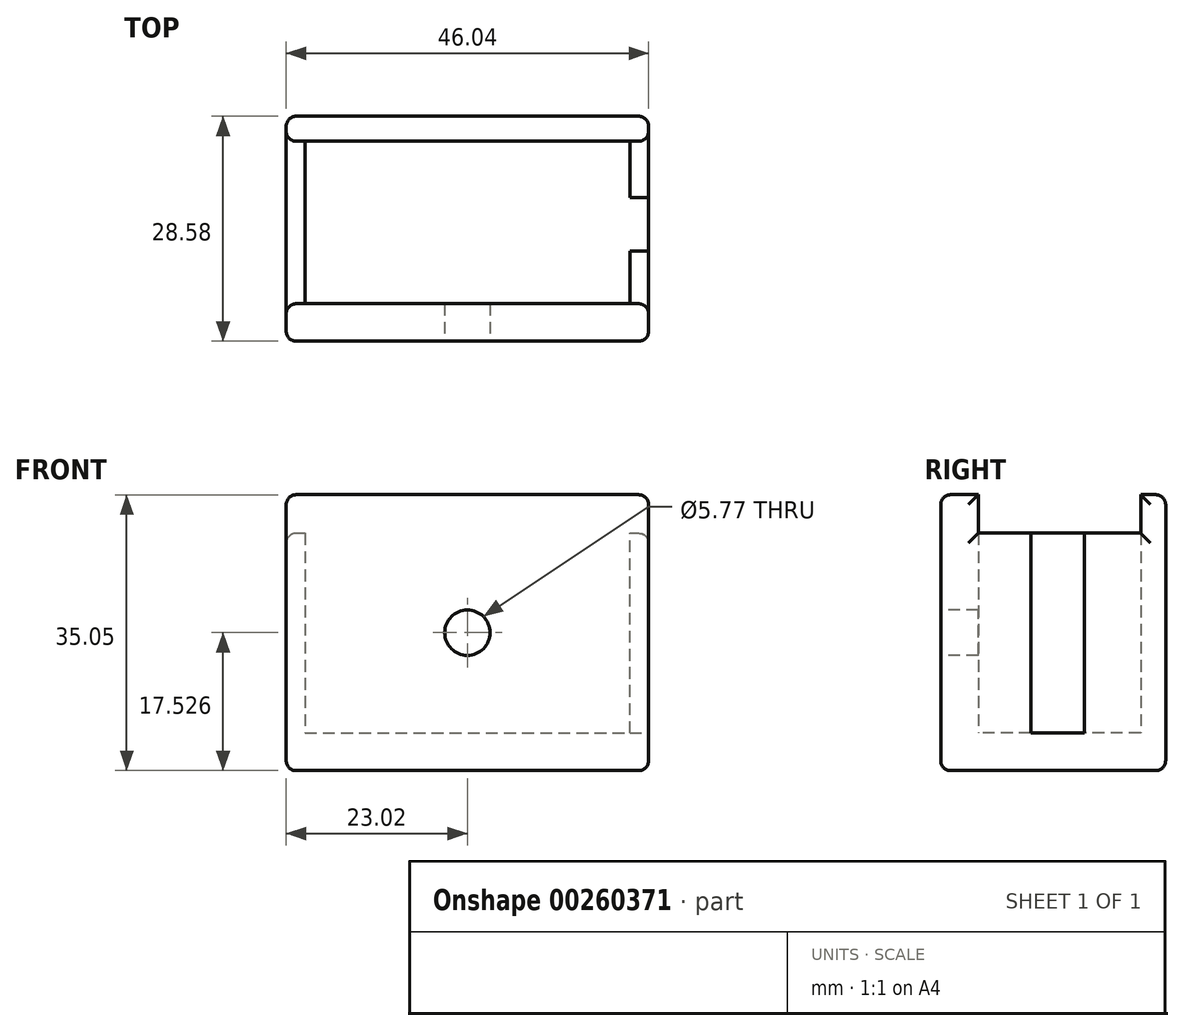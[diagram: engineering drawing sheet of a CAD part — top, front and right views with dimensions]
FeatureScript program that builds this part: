
annotation { "Feature Type Name" : "Feature", "Feature Type Description" : "" }
export const myFeature = defineFeature(function(context is Context, id is Id, definition is map)
    precondition{}
    {
        {
            var Q0;
            Q0=qCreatedBy(makeId("Top.planeOp"),FACE);
            var sketch = newSketch(context, id + "F0", { "sketchPlane" : qUnion([Q0])});
            skLineSegment(sketch, "E0.bottom", {"start": v(23.02, 14.29) * mm, "end": v(-23.02, 14.29) * mm});
            skLineSegment(sketch, "E0.top", {"start": v(23.02, -14.29) * mm, "end": v(-23.02, -14.29) * mm});
            skLineSegment(sketch, "E0.left", {"start": v(23.02, 14.29) * mm, "end": v(23.02, -14.29) * mm});
            skLineSegment(sketch, "E0.right", {"start": v(-23.02, 14.29) * mm, "end": v(-23.02, -14.29) * mm});
            skPoint(sketch, "E0.middle", {"position": v(0, 0) * mm});
            skSolve(sketch);
        }
        {
            var Q0;
            Q0=makeQuery(id+"F0.imprint","IMPRINT",FACE,{"disambiguationData":[TD([[makeQuery(id+"F0.imprint","IMPRINT",EDGE,{"derivedFrom":sQuery(id+"F0.wireOp",EDGE,"E0.bottom")}),1.0]])]});
            extrude(context, id + "F1", {"entities" : qUnion([Q0]), "depth" : 4.76 * mm});
        }
        {
            var Q0;
            Q0=makeQuery(id+"F1.opExtrude","CAP_FACE",FACE,{"disambiguationData":[OSD([sQuery(id+"F0.wireOp",EDGE,"E0.bottom"),sQuery(id+"F0.wireOp",EDGE,"E0.top"),sQuery(id+"F0.wireOp",EDGE,"E0.left"),sQuery(id+"F0.wireOp",EDGE,"E0.right")])],"isStart":false});
            var sketch = newSketch(context, id + "F2", { "sketchPlane" : qUnion([Q0])});
            skLineSegment(sketch, "E1.bottom", {"start": v(-23.02, -14.29) * mm, "end": v(23.02, -14.29) * mm});
            skLineSegment(sketch, "E1.top", {"start": v(-23.02, -9.53) * mm, "end": v(23.02, -9.53) * mm});
            skLineSegment(sketch, "E1.left", {"start": v(-23.02, -14.29) * mm, "end": v(-23.02, -9.53) * mm});
            skLineSegment(sketch, "E1.right", {"start": v(23.02, -14.29) * mm, "end": v(23.02, -9.53) * mm});
            skLineSegment(sketch, "E2.bottom", {"start": v(-23.02, 14.29) * mm, "end": v(23.02, 14.29) * mm});
            skLineSegment(sketch, "E2.top", {"start": v(-23.02, 11.11) * mm, "end": v(23.02, 11.11) * mm});
            skLineSegment(sketch, "E2.left", {"start": v(-23.02, 14.29) * mm, "end": v(-23.02, 11.11) * mm});
            skLineSegment(sketch, "E2.right", {"start": v(23.02, 14.29) * mm, "end": v(23.02, 11.11) * mm});
            skLineSegment(sketch, "E3.bottom", {"start": v(-23.02, 11.11) * mm, "end": v(-20.64, 11.11) * mm});
            skLineSegment(sketch, "E3.top", {"start": v(-23.02, -9.53) * mm, "end": v(-20.64, -9.53) * mm});
            skLineSegment(sketch, "E3.left", {"start": v(-23.02, 11.11) * mm, "end": v(-23.02, -9.53) * mm});
            skLineSegment(sketch, "E3.right", {"start": v(-20.64, 11.11) * mm, "end": v(-20.64, -9.53) * mm});
            skLineSegment(sketch, "E4.bottom", {"start": v(23.02, 11.11) * mm, "end": v(20.64, 11.11) * mm});
            skLineSegment(sketch, "E4.top", {"start": v(23.02, -9.53) * mm, "end": v(20.64, -9.53) * mm});
            skLineSegment(sketch, "E4.left", {"start": v(23.02, 11.11) * mm, "end": v(23.02, -9.53) * mm});
            skLineSegment(sketch, "E4.right", {"start": v(20.64, 11.11) * mm, "end": v(20.64, -9.53) * mm});
            skSolve(sketch);
        }
        {
            var Q0;
            Q0=makeQuery(id+"F2.imprint","IMPRINT",FACE,{"disambiguationData":[TD([[makeQuery(id+"F2.imprint","IMPRINT",EDGE,{"derivedFrom":sQuery(id+"F2.wireOp",EDGE,"E1.bottom")}),-1.0]])]});
            var Q1;
            Q1=makeQuery(id+"F2.imprint","IMPRINT",FACE,{"disambiguationData":[TD([[makeQuery(id+"F2.imprint","IMPRINT",EDGE,{"derivedFrom":sQuery(id+"F2.wireOp",EDGE,"E2.bottom")}),1.0]])]});
            extrude(context, id + "F3", {"entities" : qUnion([Q0, Q1]), "operationType" : NewBodyOperationType.ADD, "depth" : 30.29 * mm});
        }
        {
            var Q0;
            Q0 = qSketchRegion(id + "F2", true);
            extrude(context, id + "F4", {"entities" : qUnion([Q0]), "operationType" : NewBodyOperationType.ADD, "depth" : 25.4 * mm});
        }
        {
            var Q0;
            {var subQ0=sQuery(id+"F2.wireOp",EDGE,"E2.right");var subQ1=sQuery(id+"F2.wireOp",EDGE,"E1.right");Q0=makeQuery(id+"F4.boolean.opBoolean","MERGE",FACE,{"derivedFrom":[makeQuery(id+"F3.boolean.opBoolean","MERGE",FACE,{"derivedFrom":[makeQuery(id+"F1.opExtrude","SWEPT_FACE",FACE,{"disambiguationData":[OSD([sQuery(id+"F0.wireOp",EDGE,"E0.left")])]}),makeQuery(id+"F3.opExtrude","SWEPT_FACE",FACE,{"disambiguationData":[OSD([subQ1])]}),makeQuery(id+"F3.opExtrude","SWEPT_FACE",FACE,{"disambiguationData":[OSD([subQ0])]})]}),makeQuery(id+"F4.opExtrude","SWEPT_FACE",FACE,{"disambiguationData":[OSD([subQ1,subQ0,sQuery(id+"F2.wireOp",EDGE,"E4.left")])]})]});}
            var sketch = newSketch(context, id + "F5", { "sketchPlane" : qUnion([Q0])});
            skLineSegment(sketch, "E5.top", {"start": v(0.35, 30.16) * mm, "end": v(3.97, 30.16) * mm});
            skLineSegment(sketch, "E5.right", {"start": v(3.97, 16.57) * mm, "end": v(3.97, 30.16) * mm});
            skLineSegment(sketch, "E6.top", {"start": v(3.97, 4.76) * mm, "end": v(0.35, 4.76) * mm});
            skLineSegment(sketch, "E6.left", {"start": v(3.97, 16.57) * mm, "end": v(3.97, 4.76) * mm});
            skLineSegment(sketch, "E7.bottom", {"start": v(0.35, 30.16) * mm, "end": v(-2.83, 30.16) * mm});
            skLineSegment(sketch, "E7.right", {"start": v(-2.83, 30.16) * mm, "end": v(-2.83, 16.57) * mm});
            skLineSegment(sketch, "E8.top", {"start": v(0.35, 4.76) * mm, "end": v(-2.83, 4.76) * mm});
            skLineSegment(sketch, "E8.right", {"start": v(-2.83, 11.8) * mm, "end": v(-2.83, 4.76) * mm});
            skLineSegment(sketch, "E9", {"start": v(-2.83, 16.57) * mm, "end": v(-2.83, 11.8) * mm});
            skSolve(sketch);
        }
        {
            var Q0;
            Q0=makeQuery(id+"F5.imprint","IMPRINT",FACE,{"disambiguationData":[TD([[makeQuery(id+"F5.imprint","IMPRINT",EDGE,{"derivedFrom":sQuery(id+"F5.wireOp",EDGE,"sFapN1J0-1lHc-71WO-3CpR-hcseuhe5HOpb.bottom")}),-1.0]])]});
            var Q1;
            Q1=makeQuery(id+"F5.imprint","IMPRINT",FACE,{"disambiguationData":[TD([[makeQuery(id+"F5.imprint","IMPRINT",EDGE,{"derivedFrom":sQuery(id+"F5.wireOp",EDGE,"E5.top")}),1.0]])]});
            extrude(context, id + "F6", {"entities" : qUnion([Q0, Q1]), "operationType" : NewBodyOperationType.REMOVE, "endBound" : BoundingType.UP_TO_NEXT, "oppositeDirection" : true, "depth" : 25.4 * mm});
        }
        {
            var Q0;
            Q0=makeQuery(id+"F3.boolean.opBoolean","MERGE",FACE,{"derivedFrom":[makeQuery(id+"F1.opExtrude","SWEPT_FACE",FACE,{"disambiguationData":[OSD([sQuery(id+"F0.wireOp",EDGE,"E0.top")])]}),makeQuery(id+"F3.opExtrude","SWEPT_FACE",FACE,{"disambiguationData":[OSD([sQuery(id+"F2.wireOp",EDGE,"E1.bottom")])]})]});
            var sketch = newSketch(context, id + "F7", { "sketchPlane" : qUnion([Q0])});
            skLineSegment(sketch, "E10", {"start": v(-23.02, 17.53) * mm, "end": v(23.02, 17.53) * mm});
            skLineSegment(sketch, "E11", {"start": v(0, 0) * mm, "end": v(0, 35.05) * mm});
            skPoint(sketch, "E12", {"position": v(0, 17.53) * mm});
            skSolve(sketch);
        }
        {
            var Q0;
            Q0=sQuery(id+"F7.wireOp",VERTEX,"E12");
            var Q1;
            Q1=makeQuery(id+"F1.opExtrude","SWEPT_BODY",BODY,{"disambiguationData":[OSD([sQuery(id+"F0.wireOp",EDGE,"E0.bottom"),sQuery(id+"F0.wireOp",EDGE,"E0.top"),sQuery(id+"F0.wireOp",EDGE,"E0.left"),sQuery(id+"F0.wireOp",EDGE,"E0.right")])]});
            hole(context, id + "F8", {"style" : HoleStyle.SIMPLE, "endStyle" : HoleEndStyle.BLIND, "holeDiameter" : 5.77 * mm, "holeDepth" : 4.76 * mm, "tappedDepth" : 12.7 * mm, "tapClearance" : 3, "startFromSketch" : true, "locations" : qUnion([Q0]), "scope" : qUnion([Q1])});
        }
        {
            var Q0;
            Q0=makeQuery(id+"F3.boolean.opBoolean","MERGE",EDGE,{"derivedFrom":[makeQuery(id+"F1.opExtrude","SWEPT_EDGE",EDGE,{"disambiguationData":[OSD([sQuery(id+"F0.wireOp",EDGE,"E0.bottom"),sQuery(id+"F0.wireOp",EDGE,"E0.left")])]}),makeQuery(id+"F3.opExtrude","SWEPT_EDGE",EDGE,{"disambiguationData":[OSD([sQuery(id+"F2.wireOp",EDGE,"E2.bottom"),sQuery(id+"F2.wireOp",EDGE,"E2.right")])]})]});
            var Q1;
            Q1=makeQuery(id+"F3.boolean.opBoolean","MERGE",EDGE,{"derivedFrom":[makeQuery(id+"F1.opExtrude","SWEPT_EDGE",EDGE,{"disambiguationData":[OSD([sQuery(id+"F0.wireOp",EDGE,"E0.bottom"),sQuery(id+"F0.wireOp",EDGE,"E0.right")])]}),makeQuery(id+"F3.opExtrude","SWEPT_EDGE",EDGE,{"disambiguationData":[OSD([sQuery(id+"F2.wireOp",EDGE,"E2.bottom"),sQuery(id+"F2.wireOp",EDGE,"E2.left")])]})]});
            var Q2;
            Q2=makeQuery(id+"F3.opExtrude","CAP_EDGE",EDGE,{"disambiguationData":[OSD([sQuery(id+"F2.wireOp",EDGE,"E2.bottom")])],"isStart":false});
            var Q3;
            Q3=makeQuery(id+"F1.opExtrude","CAP_EDGE",EDGE,{"disambiguationData":[OSD([sQuery(id+"F0.wireOp",EDGE,"E0.bottom")])],"isStart":true});
            var Q4;
            Q4=makeQuery(id+"F1.opExtrude","CAP_EDGE",EDGE,{"disambiguationData":[OSD([sQuery(id+"F0.wireOp",EDGE,"E0.left")])],"isStart":true});
            var Q5;
            Q5=makeQuery(id+"F1.opExtrude","CAP_EDGE",EDGE,{"disambiguationData":[OSD([sQuery(id+"F0.wireOp",EDGE,"E0.right")])],"isStart":true});
            var Q6;
            Q6=makeQuery(id+"F3.opExtrude","CAP_EDGE",EDGE,{"disambiguationData":[OSD([sQuery(id+"F2.wireOp",EDGE,"E2.right")])],"isStart":false});
            var Q7;
            Q7=makeQuery(id+"F3.opExtrude","CAP_EDGE",EDGE,{"disambiguationData":[OSD([sQuery(id+"F2.wireOp",EDGE,"E2.left")])],"isStart":false});
            var Q8;
            Q8=makeQuery(id+"F3.boolean.opBoolean","MERGE",EDGE,{"derivedFrom":[makeQuery(id+"F1.opExtrude","SWEPT_EDGE",EDGE,{"disambiguationData":[OSD([sQuery(id+"F0.wireOp",EDGE,"E0.top"),sQuery(id+"F0.wireOp",EDGE,"E0.left")])]}),makeQuery(id+"F3.opExtrude","SWEPT_EDGE",EDGE,{"disambiguationData":[OSD([sQuery(id+"F2.wireOp",EDGE,"E1.bottom"),sQuery(id+"F2.wireOp",EDGE,"E1.right")])]})]});
            var Q9;
            Q9=makeQuery(id+"F3.opExtrude","CAP_EDGE",EDGE,{"disambiguationData":[OSD([sQuery(id+"F2.wireOp",EDGE,"E1.bottom")])],"isStart":false});
            var Q10;
            Q10=makeQuery(id+"F3.boolean.opBoolean","MERGE",EDGE,{"derivedFrom":[makeQuery(id+"F1.opExtrude","SWEPT_EDGE",EDGE,{"disambiguationData":[OSD([sQuery(id+"F0.wireOp",EDGE,"E0.top"),sQuery(id+"F0.wireOp",EDGE,"E0.right")])]}),makeQuery(id+"F3.opExtrude","SWEPT_EDGE",EDGE,{"disambiguationData":[OSD([sQuery(id+"F2.wireOp",EDGE,"E1.bottom"),sQuery(id+"F2.wireOp",EDGE,"E1.left")])]})]});
            var Q11;
            Q11=makeQuery(id+"F1.opExtrude","CAP_EDGE",EDGE,{"disambiguationData":[OSD([sQuery(id+"F0.wireOp",EDGE,"E0.top")])],"isStart":true});
            var Q12;
            Q12=makeQuery(id+"F3.opExtrude","CAP_EDGE",EDGE,{"disambiguationData":[OSD([sQuery(id+"F2.wireOp",EDGE,"E1.right")])],"isStart":false});
            var Q13;
            Q13=makeQuery(id+"F3.opExtrude","CAP_EDGE",EDGE,{"disambiguationData":[OSD([sQuery(id+"F2.wireOp",EDGE,"E1.left")])],"isStart":false});
            var Q14;
            Q14=makeQuery(id+"F4.opExtrude","CAP_EDGE",EDGE,{"disambiguationData":[OSD([sQuery(id+"F2.wireOp",EDGE,"E1.left"),sQuery(id+"F2.wireOp",EDGE,"E2.left"),sQuery(id+"F2.wireOp",EDGE,"E3.left")])],"isStart":false});
            var Q15;
            {var subQ0=sQuery(id+"F2.wireOp",EDGE,"E2.right");var subQ2=sQuery(id+"F2.wireOp",EDGE,"E4.left");var subQ3=sQuery(id+"F2.wireOp",EDGE,"E1.right");Q15=makeQuery(id+"F6.boolean.opBoolean","SPLIT",EDGE,{"disambiguationData":[TD([makeQuery(id+"F6.opExtrude","SWEPT_FACE",FACE,{"disambiguationData":[OSD([sQuery(id+"F5.wireOp",EDGE,"E5.right"),sQuery(id+"F5.wireOp",EDGE,"E6.left")])]})])],"derivedFrom":makeQuery(id+"F4.opExtrude","CAP_EDGE",EDGE,{"disambiguationData":[OSD([subQ3,subQ0,subQ2])],"isStart":false})});}
            var Q16;
            {var subQ0=sQuery(id+"F2.wireOp",EDGE,"E2.right");var subQ1=sQuery(id+"F2.wireOp",EDGE,"E1.top");var subQ2=sQuery(id+"F2.wireOp",EDGE,"E1.right");var subQ3=sQuery(id+"F2.wireOp",EDGE,"E4.left");Q16=makeQuery(id+"F6.boolean.opBoolean","SPLIT",EDGE,{"disambiguationData":[TD([makeQuery(id+"F3.opExtrude","SWEPT_FACE",FACE,{"disambiguationData":[OSD([subQ1,sQuery(id+"F2.wireOp",EDGE,"E3.top"),sQuery(id+"F2.wireOp",EDGE,"E4.top")])]})])],"derivedFrom":makeQuery(id+"F4.opExtrude","CAP_EDGE",EDGE,{"disambiguationData":[OSD([subQ2,subQ0,subQ3])],"isStart":false})});}
            var Q17;
            Q17=makeQuery(id+"F3.opExtrude","SWEPT_EDGE",EDGE,{"disambiguationData":[OSD([sQuery(id+"F2.wireOp",EDGE,"E1.right"),sQuery(id+"F2.wireOp",EDGE,"E4.top"),sQuery(id+"F2.wireOp",EDGE,"E4.left")])]});
            var Q18;
            Q18=makeQuery(id+"F3.opExtrude","SWEPT_EDGE",EDGE,{"disambiguationData":[OSD([sQuery(id+"F2.wireOp",EDGE,"E1.left"),sQuery(id+"F2.wireOp",EDGE,"E3.top"),sQuery(id+"F2.wireOp",EDGE,"E3.left")])]});
            var Q19;
            Q19=makeQuery(id+"F3.opExtrude","SWEPT_EDGE",EDGE,{"disambiguationData":[OSD([sQuery(id+"F2.wireOp",EDGE,"E2.left"),sQuery(id+"F2.wireOp",EDGE,"E3.bottom"),sQuery(id+"F2.wireOp",EDGE,"E3.left")])]});
            var Q20;
            Q20=makeQuery(id+"F3.opExtrude","SWEPT_EDGE",EDGE,{"disambiguationData":[OSD([sQuery(id+"F2.wireOp",EDGE,"E2.right"),sQuery(id+"F2.wireOp",EDGE,"E4.bottom"),sQuery(id+"F2.wireOp",EDGE,"E4.left")])]});
            fillet(context, id + "F9", {"entities" : qUnion([Q0, Q1, Q2, Q3, Q4, Q5, Q6, Q7, Q8, Q9, Q10, Q11, Q12, Q13, Q14, Q15, Q16, Q17, Q18, Q19, Q20]), "radius" : 1.27 * mm, "tangentPropagation" : true, "allowEdgeOverflow" : false});
        }
    });
